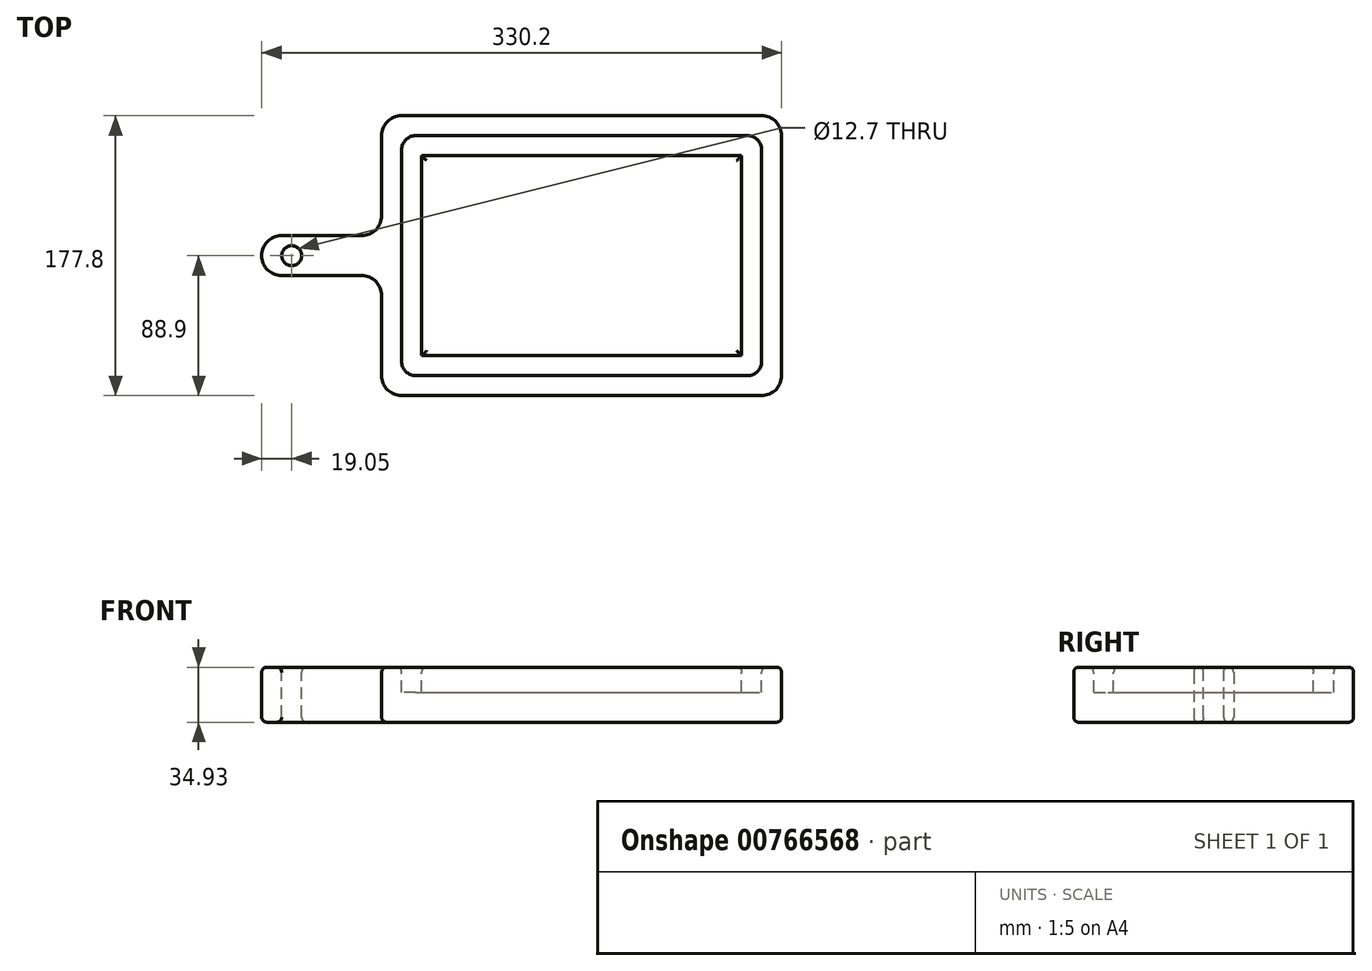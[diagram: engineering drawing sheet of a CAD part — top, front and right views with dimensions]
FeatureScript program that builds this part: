
annotation { "Feature Type Name" : "Feature", "Feature Type Description" : "" }
export const myFeature = defineFeature(function(context is Context, id is Id, definition is map)
    precondition{}
    {
        {
            var Q0;
            Q0=qCreatedBy(makeId("Top.planeOp"),FACE);
            var sketch = newSketch(context, id + "F0", { "sketchPlane" : qUnion([Q0])});
            skLineSegment(sketch, "E0.bottom", {"start": v(0, 0) * mm, "end": v(254, 0) * mm});
            skLineSegment(sketch, "E0.top", {"start": v(0, 177.8) * mm, "end": v(254, 177.8) * mm});
            skLineSegment(sketch, "E0.left", {"start": v(0, 0) * mm, "end": v(0, 177.8) * mm});
            skLineSegment(sketch, "E0.right", {"start": v(254, 0) * mm, "end": v(254, 177.8) * mm});
            skLineSegment(sketch, "E1.bottom", {"start": v(0, 101.6) * mm, "end": v(-76.2, 101.6) * mm});
            skLineSegment(sketch, "E1.top", {"start": v(0, 76.2) * mm, "end": v(-76.2, 76.2) * mm});
            skLineSegment(sketch, "E1.left", {"start": v(0, 101.6) * mm, "end": v(0, 76.2) * mm});
            skLineSegment(sketch, "E1.right", {"start": v(-76.2, 101.6) * mm, "end": v(-76.2, 76.2) * mm});
            skSolve(sketch);
        }
        {
            var Q0;
            {var subQ3=sQuery(id+"F0.wireOp",EDGE,"E0.bottom");Q0=makeQuery(id+"F0.imprint","IMPRINT",FACE,{"disambiguationData":[TD([[makeQuery(id+"F0.imprint","IMPRINT",EDGE,{"derivedFrom":subQ3}),1.0]])]});}
            var Q1;
            Q1=makeQuery(id+"F0.imprint","IMPRINT",FACE,{"disambiguationData":[TD([[makeQuery(id+"F0.imprint","IMPRINT",EDGE,{"derivedFrom":sQuery(id+"F0.wireOp",EDGE,"E1.bottom")}),1.0]])]});
            extrude(context, id + "F1", {"entities" : qUnion([Q0, Q1]), "depth" : 25.4 * mm, "offsetDistance" : 25.4 * mm});
        }
        {
            var Q0;
            Q0=makeQuery(id+"F1.opExtrude","CAP_FACE",FACE,{"disambiguationData":[OSD([sQuery(id+"F0.wireOp",EDGE,"E0.bottom"),sQuery(id+"F0.wireOp",EDGE,"E0.top"),sQuery(id+"F0.wireOp",EDGE,"E0.left"),sQuery(id+"F0.wireOp",EDGE,"E0.right"),sQuery(id+"F0.wireOp",EDGE,"E1.bottom"),sQuery(id+"F0.wireOp",EDGE,"E1.top"),sQuery(id+"F0.wireOp",EDGE,"E1.right")])],"isStart":false});
            var sketch = newSketch(context, id + "F2", { "sketchPlane" : qUnion([Q0])});
            skCircle(sketch, "E2", {"center": v(-57.15, 88.9) * mm, "radius": 6.35 * mm});
            skSolve(sketch);
        }
        {
            var Q0;
            Q0 = qSketchRegion(id + "F2", true);
            extrude(context, id + "F3", {"entities" : qUnion([Q0]), "operationType" : NewBodyOperationType.REMOVE, "oppositeDirection" : true, "depth" : 25.4 * mm, "offsetDistance" : 25.4 * mm});
        }
        {
            var Q0;
            Q0=makeQuery(id+"F1.opExtrude","CAP_FACE",FACE,{"disambiguationData":[OSD([sQuery(id+"F0.wireOp",EDGE,"E0.bottom"),sQuery(id+"F0.wireOp",EDGE,"E0.top"),sQuery(id+"F0.wireOp",EDGE,"E0.left"),sQuery(id+"F0.wireOp",EDGE,"E0.right"),sQuery(id+"F0.wireOp",EDGE,"E1.bottom"),sQuery(id+"F0.wireOp",EDGE,"E1.top"),sQuery(id+"F0.wireOp",EDGE,"E1.right")])],"isStart":false});
            var sketch = newSketch(context, id + "F4", { "sketchPlane" : qUnion([Q0])});
            skLineSegment(sketch, "E3.0", {"start": v(12.7, 12.7) * mm, "end": v(12.7, 76.2) * mm});
            skLineSegment(sketch, "E3.1", {"start": v(12.7, 101.6) * mm, "end": v(12.7, 165.1) * mm});
            skLineSegment(sketch, "E3.2", {"start": v(12.7, 165.1) * mm, "end": v(241.3, 165.1) * mm});
            skLineSegment(sketch, "E3.3", {"start": v(241.3, 12.7) * mm, "end": v(241.3, 165.1) * mm});
            skLineSegment(sketch, "E3.4", {"start": v(12.7, 12.7) * mm, "end": v(241.3, 12.7) * mm});
            skLineSegment(sketch, "E4", {"start": v(12.7, 101.6) * mm, "end": v(12.7, 76.2) * mm});
            skLineSegment(sketch, "E5.0", {"start": v(25.4, 101.6) * mm, "end": v(25.4, 152.4) * mm});
            skLineSegment(sketch, "E5.1", {"start": v(228.6, 25.4) * mm, "end": v(228.6, 152.4) * mm});
            skLineSegment(sketch, "E5.2", {"start": v(25.4, 25.4) * mm, "end": v(228.6, 25.4) * mm});
            skLineSegment(sketch, "E5.3", {"start": v(25.4, 152.4) * mm, "end": v(228.6, 152.4) * mm});
            skLineSegment(sketch, "E5.4", {"start": v(25.4, 25.4) * mm, "end": v(25.4, 76.2) * mm});
            skLineSegment(sketch, "E5.5", {"start": v(25.4, 101.6) * mm, "end": v(25.4, 76.2) * mm});
            skSolve(sketch);
        }
        {
            var Q0;
            Q0=makeQuery(id+"F4.imprint","IMPRINT",FACE,{"disambiguationData":[TD([[makeQuery(id+"F4.imprint","IMPRINT",EDGE,{"derivedFrom":sQuery(id+"F4.wireOp",EDGE,"E3.0")}),-1.0]])]});
            extrude(context, id + "F5", {"entities" : qUnion([Q0]), "operationType" : NewBodyOperationType.REMOVE, "oppositeDirection" : true, "depth" : 6.35 * mm, "offsetDistance" : 25.4 * mm});
        }
        {
            var Q0;
            Q0=makeQuery(id+"F5.boolean.opBoolean","COPY",EDGE,{"derivedFrom":makeQuery(id+"F5.opExtrude","SWEPT_EDGE",EDGE,{"disambiguationData":[OSD([sQuery(id+"F4.wireOp",EDGE,"E3.1"),sQuery(id+"F4.wireOp",EDGE,"E3.2")])]})});
            var Q1;
            Q1=makeQuery(id+"F5.boolean.opBoolean","COPY",EDGE,{"derivedFrom":makeQuery(id+"F5.opExtrude","SWEPT_EDGE",EDGE,{"disambiguationData":[OSD([sQuery(id+"F4.wireOp",EDGE,"E3.2"),sQuery(id+"F4.wireOp",EDGE,"E3.3")])]})});
            var Q2;
            Q2=makeQuery(id+"F5.boolean.opBoolean","COPY",EDGE,{"derivedFrom":makeQuery(id+"F5.opExtrude","SWEPT_EDGE",EDGE,{"disambiguationData":[OSD([sQuery(id+"F4.wireOp",EDGE,"E3.0"),sQuery(id+"F4.wireOp",EDGE,"E3.4")])]})});
            var Q3;
            Q3=makeQuery(id+"F5.boolean.opBoolean","COPY",EDGE,{"derivedFrom":makeQuery(id+"F5.opExtrude","SWEPT_EDGE",EDGE,{"disambiguationData":[OSD([sQuery(id+"F4.wireOp",EDGE,"E3.3"),sQuery(id+"F4.wireOp",EDGE,"E3.4")])]})});
            fillet(context, id + "F6", {"entities" : qUnion([Q0, Q1, Q2, Q3]), "radius" : 8.9 * mm, "tangentPropagation" : true, "allowEdgeOverflow" : false});
        }
        {
            var Q0;
            Q0=makeQuery(id+"F1.opExtrude","SWEPT_EDGE",EDGE,{"disambiguationData":[OSD([sQuery(id+"F0.wireOp",EDGE,"E0.bottom"),sQuery(id+"F0.wireOp",EDGE,"E0.left")])]});
            var Q1;
            Q1=makeQuery(id+"F1.opExtrude","SWEPT_EDGE",EDGE,{"disambiguationData":[OSD([sQuery(id+"F0.wireOp",EDGE,"E1.bottom"),sQuery(id+"F0.wireOp",EDGE,"E1.right")])]});
            var Q2;
            Q2=makeQuery(id+"F1.opExtrude","SWEPT_EDGE",EDGE,{"disambiguationData":[OSD([sQuery(id+"F0.wireOp",EDGE,"E1.top"),sQuery(id+"F0.wireOp",EDGE,"E1.right")])]});
            var Q3;
            Q3=makeQuery(id+"F1.opExtrude","SWEPT_EDGE",EDGE,{"disambiguationData":[OSD([sQuery(id+"F0.wireOp",EDGE,"E0.left"),sQuery(id+"F0.wireOp",EDGE,"E1.top"),sQuery(id+"F0.wireOp",EDGE,"E1.left")])]});
            var Q4;
            Q4=makeQuery(id+"F1.opExtrude","SWEPT_EDGE",EDGE,{"disambiguationData":[OSD([sQuery(id+"F0.wireOp",EDGE,"E0.top"),sQuery(id+"F0.wireOp",EDGE,"E0.right")])]});
            var Q5;
            Q5=makeQuery(id+"F1.opExtrude","SWEPT_EDGE",EDGE,{"disambiguationData":[OSD([sQuery(id+"F0.wireOp",EDGE,"E0.bottom"),sQuery(id+"F0.wireOp",EDGE,"E0.right")])]});
            var Q6;
            Q6=makeQuery(id+"F1.opExtrude","SWEPT_EDGE",EDGE,{"disambiguationData":[OSD([sQuery(id+"F0.wireOp",EDGE,"E0.left"),sQuery(id+"F0.wireOp",EDGE,"E1.bottom"),sQuery(id+"F0.wireOp",EDGE,"E1.left")])]});
            var Q7;
            Q7=makeQuery(id+"F1.opExtrude","SWEPT_EDGE",EDGE,{"disambiguationData":[OSD([sQuery(id+"F0.wireOp",EDGE,"E0.top"),sQuery(id+"F0.wireOp",EDGE,"E0.left")])]});
            fillet(context, id + "F7", {"entities" : qUnion([Q0, Q1, Q2, Q3, Q4, Q5, Q6, Q7]), "radius" : 12.7 * mm, "tangentPropagation" : true, "allowEdgeOverflow" : false});
        }
        {
            var Q0;
            Q0=makeQuery(id+"F5.boolean.opBoolean","SPLIT",FACE,{"disambiguationData":[TD([makeQuery(id+"F5.opExtrude","SWEPT_FACE",FACE,{"disambiguationData":[OSD([sQuery(id+"F4.wireOp",EDGE,"E5.1")])]})])],"derivedFrom":makeQuery(id+"F1.opExtrude","CAP_FACE",FACE,{"disambiguationData":[OSD([sQuery(id+"F0.wireOp",EDGE,"E0.bottom"),sQuery(id+"F0.wireOp",EDGE,"E0.top"),sQuery(id+"F0.wireOp",EDGE,"E0.left"),sQuery(id+"F0.wireOp",EDGE,"E0.right"),sQuery(id+"F0.wireOp",EDGE,"E1.bottom"),sQuery(id+"F0.wireOp",EDGE,"E1.top"),sQuery(id+"F0.wireOp",EDGE,"E1.right")])],"isStart":false})});
            var Q1;
            {var subQ0=sQuery(id+"F0.wireOp",EDGE,"E0.left");var subQ1=sQuery(id+"F0.wireOp",EDGE,"E0.top");var subQ3=sQuery(id+"F0.wireOp",EDGE,"E1.bottom");var subQ4=sQuery(id+"F0.wireOp",EDGE,"E1.right");var subQ5=sQuery(id+"F0.wireOp",EDGE,"E1.top");var subQ6=sQuery(id+"F0.wireOp",EDGE,"E0.right");var subQ7=sQuery(id+"F0.wireOp",EDGE,"E0.bottom");Q1=makeQuery(id+"F5.boolean.opBoolean","SPLIT",FACE,{"disambiguationData":[TD([makeQuery(id+"F1.opExtrude","SWEPT_FACE",FACE,{"disambiguationData":[OSD([subQ7])]})])],"derivedFrom":makeQuery(id+"F1.opExtrude","CAP_FACE",FACE,{"disambiguationData":[OSD([subQ7,subQ1,subQ0,subQ6,subQ3,subQ5,subQ4])],"isStart":false})});}
            var Q2;
            Q2=makeQuery(id+"F1.opExtrude","CAP_FACE",FACE,{"disambiguationData":[OSD([sQuery(id+"F0.wireOp",EDGE,"E0.bottom"),sQuery(id+"F0.wireOp",EDGE,"E0.top"),sQuery(id+"F0.wireOp",EDGE,"E0.left"),sQuery(id+"F0.wireOp",EDGE,"E0.right"),sQuery(id+"F0.wireOp",EDGE,"E1.bottom"),sQuery(id+"F0.wireOp",EDGE,"E1.top"),sQuery(id+"F0.wireOp",EDGE,"E1.right")])],"isStart":true});
            extrude(context, id + "F8", {"entities" : qUnion([Q0, Q1, Q2]), "operationType" : NewBodyOperationType.ADD, "depth" : 3.17 * mm, "offsetDistance" : 25.4 * mm});
        }
        {
            var Q0;
            {var subQ0=sQuery(id+"F0.wireOp",EDGE,"E1.right");var subQ1=sQuery(id+"F0.wireOp",EDGE,"E1.top");var subQ2=sQuery(id+"F0.wireOp",EDGE,"E1.bottom");var subQ3=sQuery(id+"F0.wireOp",EDGE,"E0.right");var subQ4=sQuery(id+"F0.wireOp",EDGE,"E0.left");var subQ5=sQuery(id+"F0.wireOp",EDGE,"E0.top");var subQ6=sQuery(id+"F0.wireOp",EDGE,"E0.bottom");Q0=makeQuery(id+"F8.opExtrude","CAP_FACE",FACE,{"disambiguationData":[OSD([subQ6,subQ5,subQ4,subQ3,subQ2,subQ1,subQ0]),TDD([makeQuery(id+"F5.boolean.opBoolean","SPLIT",FACE,{"disambiguationData":[TD([makeQuery(id+"F5.opExtrude","SWEPT_FACE",FACE,{"disambiguationData":[OSD([sQuery(id+"F4.wireOp",EDGE,"E5.1")])]})])],"derivedFrom":makeQuery(id+"F1.opExtrude","CAP_FACE",FACE,{"disambiguationData":[OSD([subQ6,subQ5,subQ4,subQ3,subQ2,subQ1,subQ0])],"isStart":false})})])],"isStart":false});}
            var Q1;
            {var subQ0=sQuery(id+"F0.wireOp",EDGE,"E0.left");var subQ1=sQuery(id+"F0.wireOp",EDGE,"E0.top");var subQ3=sQuery(id+"F0.wireOp",EDGE,"E1.bottom");var subQ4=sQuery(id+"F0.wireOp",EDGE,"E1.right");var subQ5=sQuery(id+"F0.wireOp",EDGE,"E1.top");var subQ6=sQuery(id+"F0.wireOp",EDGE,"E0.right");var subQ7=sQuery(id+"F0.wireOp",EDGE,"E0.bottom");Q1=makeQuery(id+"F8.opExtrude","CAP_FACE",FACE,{"disambiguationData":[OSD([subQ7,subQ1,subQ0,subQ6,subQ3,subQ5,subQ4]),TDD([makeQuery(id+"F5.boolean.opBoolean","SPLIT",FACE,{"disambiguationData":[TD([makeQuery(id+"F1.opExtrude","SWEPT_FACE",FACE,{"disambiguationData":[OSD([subQ7])]})])],"derivedFrom":makeQuery(id+"F1.opExtrude","CAP_FACE",FACE,{"disambiguationData":[OSD([subQ7,subQ1,subQ0,subQ6,subQ3,subQ5,subQ4])],"isStart":false})})])],"isStart":false});}
            var Q2;
            Q2=makeQuery(id+"F1.opExtrude","CAP_FACE",FACE,{"disambiguationData":[OSD([sQuery(id+"F0.wireOp",EDGE,"E0.bottom"),sQuery(id+"F0.wireOp",EDGE,"E0.top"),sQuery(id+"F0.wireOp",EDGE,"E0.left"),sQuery(id+"F0.wireOp",EDGE,"E0.right"),sQuery(id+"F0.wireOp",EDGE,"E1.bottom"),sQuery(id+"F0.wireOp",EDGE,"E1.top"),sQuery(id+"F0.wireOp",EDGE,"E1.right")])],"isStart":true});
            extrude(context, id + "F9", {"entities" : qUnion([Q0, Q1, Q2]), "operationType" : NewBodyOperationType.ADD, "depth" : 3.17 * mm, "offsetDistance" : 25.4 * mm});
        }
        {
            var Q0;
            {var subQ0=sQuery(id+"F0.wireOp",EDGE,"E1.right");var subQ1=sQuery(id+"F0.wireOp",EDGE,"E1.top");var subQ2=sQuery(id+"F0.wireOp",EDGE,"E1.bottom");var subQ3=sQuery(id+"F0.wireOp",EDGE,"E0.right");var subQ4=sQuery(id+"F0.wireOp",EDGE,"E0.left");var subQ5=sQuery(id+"F0.wireOp",EDGE,"E0.top");var subQ6=sQuery(id+"F0.wireOp",EDGE,"E0.bottom");Q0=makeQuery(id+"F9.opExtrude","CAP_FACE",FACE,{"disambiguationData":[OSD([subQ6,subQ5,subQ4,subQ3,subQ2,subQ1,subQ0]),TDD([makeQuery(id+"F8.opExtrude","CAP_FACE",FACE,{"disambiguationData":[OSD([subQ6,subQ5,subQ4,subQ3,subQ2,subQ1,subQ0]),TDD([makeQuery(id+"F5.boolean.opBoolean","SPLIT",FACE,{"disambiguationData":[TD([makeQuery(id+"F5.opExtrude","SWEPT_FACE",FACE,{"disambiguationData":[OSD([sQuery(id+"F4.wireOp",EDGE,"E5.1")])]})])],"derivedFrom":makeQuery(id+"F1.opExtrude","CAP_FACE",FACE,{"disambiguationData":[OSD([subQ6,subQ5,subQ4,subQ3,subQ2,subQ1,subQ0])],"isStart":false})})])],"isStart":false})])],"isStart":false});}
            var Q1;
            {var subQ0=sQuery(id+"F0.wireOp",EDGE,"E0.left");var subQ1=sQuery(id+"F0.wireOp",EDGE,"E0.top");var subQ3=sQuery(id+"F0.wireOp",EDGE,"E1.bottom");var subQ4=sQuery(id+"F0.wireOp",EDGE,"E1.right");var subQ5=sQuery(id+"F0.wireOp",EDGE,"E1.top");var subQ6=sQuery(id+"F0.wireOp",EDGE,"E0.right");var subQ7=sQuery(id+"F0.wireOp",EDGE,"E0.bottom");Q1=makeQuery(id+"F9.opExtrude","CAP_FACE",FACE,{"disambiguationData":[OSD([subQ7,subQ1,subQ0,subQ6,subQ3,subQ5,subQ4]),TDD([makeQuery(id+"F8.opExtrude","CAP_FACE",FACE,{"disambiguationData":[OSD([subQ7,subQ1,subQ0,subQ6,subQ3,subQ5,subQ4]),TDD([makeQuery(id+"F5.boolean.opBoolean","SPLIT",FACE,{"disambiguationData":[TD([makeQuery(id+"F1.opExtrude","SWEPT_FACE",FACE,{"disambiguationData":[OSD([subQ7])]})])],"derivedFrom":makeQuery(id+"F1.opExtrude","CAP_FACE",FACE,{"disambiguationData":[OSD([subQ7,subQ1,subQ0,subQ6,subQ3,subQ5,subQ4])],"isStart":false})})])],"isStart":false})])],"isStart":false});}
            var Q2;
            Q2=makeQuery(id+"F1.opExtrude","CAP_FACE",FACE,{"disambiguationData":[OSD([sQuery(id+"F0.wireOp",EDGE,"E0.bottom"),sQuery(id+"F0.wireOp",EDGE,"E0.top"),sQuery(id+"F0.wireOp",EDGE,"E0.left"),sQuery(id+"F0.wireOp",EDGE,"E0.right"),sQuery(id+"F0.wireOp",EDGE,"E1.bottom"),sQuery(id+"F0.wireOp",EDGE,"E1.top"),sQuery(id+"F0.wireOp",EDGE,"E1.right")])],"isStart":true});
            extrude(context, id + "F10", {"entities" : qUnion([Q0, Q1, Q2]), "operationType" : NewBodyOperationType.ADD, "depth" : 3.17 * mm, "offsetDistance" : 25.4 * mm});
        }
        {
            var Q0;
            Q0=makeQuery(id+"F1.opExtrude","CAP_FACE",FACE,{"disambiguationData":[OSD([sQuery(id+"F0.wireOp",EDGE,"E0.bottom"),sQuery(id+"F0.wireOp",EDGE,"E0.top"),sQuery(id+"F0.wireOp",EDGE,"E0.left"),sQuery(id+"F0.wireOp",EDGE,"E0.right"),sQuery(id+"F0.wireOp",EDGE,"E1.bottom"),sQuery(id+"F0.wireOp",EDGE,"E1.top"),sQuery(id+"F0.wireOp",EDGE,"E1.right")])],"isStart":true});
            var Q1;
            {var subQ0=sQuery(id+"F0.wireOp",EDGE,"E1.right");var subQ1=sQuery(id+"F0.wireOp",EDGE,"E1.top");var subQ2=sQuery(id+"F0.wireOp",EDGE,"E1.bottom");var subQ3=sQuery(id+"F0.wireOp",EDGE,"E0.right");var subQ4=sQuery(id+"F0.wireOp",EDGE,"E0.left");var subQ5=sQuery(id+"F0.wireOp",EDGE,"E0.top");var subQ6=sQuery(id+"F0.wireOp",EDGE,"E0.bottom");Q1=makeQuery(id+"F10.opExtrude","CAP_FACE",FACE,{"disambiguationData":[OSD([subQ6,subQ5,subQ4,subQ3,subQ2,subQ1,subQ0]),TDD([makeQuery(id+"F9.opExtrude","CAP_FACE",FACE,{"disambiguationData":[OSD([subQ6,subQ5,subQ4,subQ3,subQ2,subQ1,subQ0]),TDD([makeQuery(id+"F8.opExtrude","CAP_FACE",FACE,{"disambiguationData":[OSD([subQ6,subQ5,subQ4,subQ3,subQ2,subQ1,subQ0]),TDD([makeQuery(id+"F5.boolean.opBoolean","SPLIT",FACE,{"disambiguationData":[TD([makeQuery(id+"F5.opExtrude","SWEPT_FACE",FACE,{"disambiguationData":[OSD([sQuery(id+"F4.wireOp",EDGE,"E5.1")])]})])],"derivedFrom":makeQuery(id+"F1.opExtrude","CAP_FACE",FACE,{"disambiguationData":[OSD([subQ6,subQ5,subQ4,subQ3,subQ2,subQ1,subQ0])],"isStart":false})})])],"isStart":false})])],"isStart":false})])],"isStart":false});}
            var Q2;
            {var subQ0=sQuery(id+"F0.wireOp",EDGE,"E0.left");var subQ1=sQuery(id+"F0.wireOp",EDGE,"E0.top");var subQ3=sQuery(id+"F0.wireOp",EDGE,"E1.bottom");var subQ4=sQuery(id+"F0.wireOp",EDGE,"E1.right");var subQ5=sQuery(id+"F0.wireOp",EDGE,"E1.top");var subQ6=sQuery(id+"F0.wireOp",EDGE,"E0.right");var subQ7=sQuery(id+"F0.wireOp",EDGE,"E0.bottom");Q2=makeQuery(id+"F10.opExtrude","CAP_FACE",FACE,{"disambiguationData":[OSD([subQ7,subQ1,subQ0,subQ6,subQ3,subQ5,subQ4]),TDD([makeQuery(id+"F9.opExtrude","CAP_FACE",FACE,{"disambiguationData":[OSD([subQ7,subQ1,subQ0,subQ6,subQ3,subQ5,subQ4]),TDD([makeQuery(id+"F8.opExtrude","CAP_FACE",FACE,{"disambiguationData":[OSD([subQ7,subQ1,subQ0,subQ6,subQ3,subQ5,subQ4]),TDD([makeQuery(id+"F5.boolean.opBoolean","SPLIT",FACE,{"disambiguationData":[TD([makeQuery(id+"F1.opExtrude","SWEPT_FACE",FACE,{"disambiguationData":[OSD([subQ7])]})])],"derivedFrom":makeQuery(id+"F1.opExtrude","CAP_FACE",FACE,{"disambiguationData":[OSD([subQ7,subQ1,subQ0,subQ6,subQ3,subQ5,subQ4])],"isStart":false})})])],"isStart":false})])],"isStart":false})])],"isStart":false});}
            fillet(context, id + "F11", {"entities" : qUnion([Q0, Q1, Q2]), "radius" : 3.17 * mm, "tangentPropagation" : true, "allowEdgeOverflow" : false});
        }
    });
